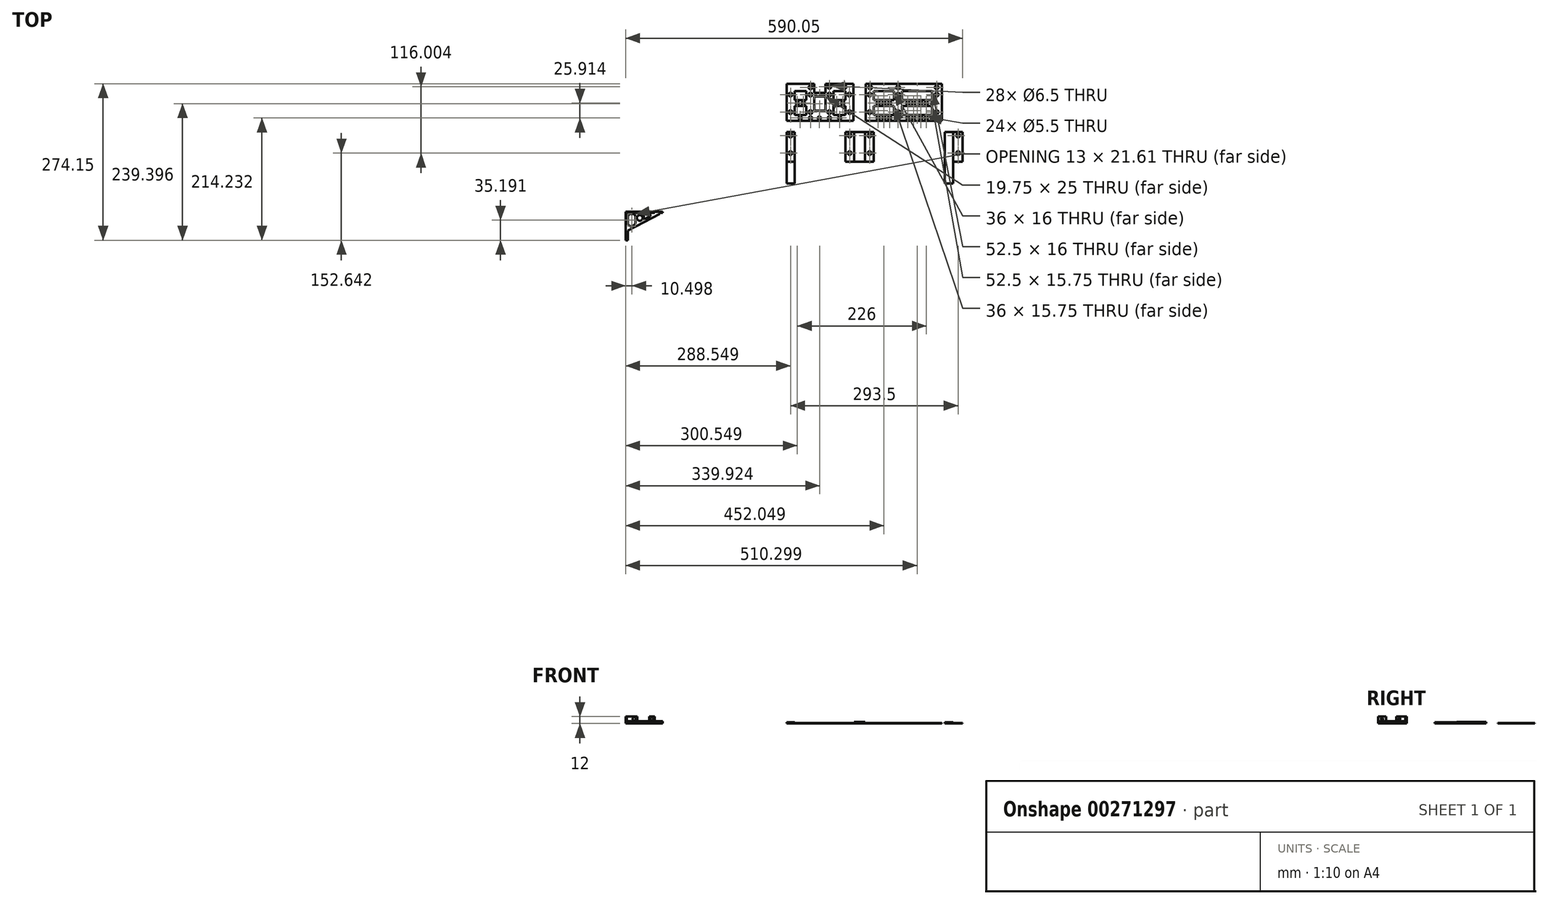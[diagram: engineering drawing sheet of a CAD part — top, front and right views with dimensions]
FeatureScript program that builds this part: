
annotation { "Feature Type Name" : "Feature", "Feature Type Description" : "" }
export const myFeature = defineFeature(function(context is Context, id is Id, definition is map)
    precondition{}
    {
        {
            var Q0;
            Q0=qCreatedBy(makeId("Top.planeOp"),FACE);
            var sketch = newSketch(context, id + "F0", { "sketchPlane" : qUnion([Q0])});
            skLineSegment(sketch, "E0.bottom", {"start": v(-67.64, 28.29) * mm, "end": v(65.86, 28.29) * mm});
            skLineSegment(sketch, "E0.left", {"start": v(-67.64, 28.29) * mm, "end": v(-67.64, 15.29) * mm});
            skLineSegment(sketch, "E0.right", {"start": v(65.86, 28.29) * mm, "end": v(65.86, 15.29) * mm});
            skCircle(sketch, "E1", {"center": v(-59.64, 21.79) * mm, "radius": 3.25 * mm});
            skCircle(sketch, "E2", {"center": v(-10.64, 21.79) * mm, "radius": 3.25 * mm});
            skCircle(sketch, "E3", {"center": v(56.86, 21.79) * mm, "radius": 3.25 * mm});
            skLineSegment(sketch, "E4.right", {"start": v(-206.14, 28.29) * mm, "end": v(-206.14, 15.29) * mm});
            skCircle(sketch, "E5", {"center": v(-164.14, 21.79) * mm, "radius": 3.25 * mm});
            skCircle(sketch, "E6", {"center": v(-131.14, 22.79) * mm, "radius": 3.25 * mm});
            skCircle(sketch, "E7", {"center": v(-104.64, 22.59) * mm, "radius": 3.25 * mm});
            skLineSegment(sketch, "E8.bottom", {"start": v(-17.64, 15.29) * mm, "end": v(-3.64, 15.29) * mm});
            skLineSegment(sketch, "E8.top", {"start": v(-17.64, -26.46) * mm, "end": v(-3.64, -26.46) * mm});
            skLineSegment(sketch, "E8.left", {"start": v(-17.64, 15.29) * mm, "end": v(-17.64, -26.46) * mm});
            skLineSegment(sketch, "E8.right", {"start": v(-3.64, 15.29) * mm, "end": v(-3.64, -26.46) * mm});
            skLineSegment(sketch, "E9.bottom", {"start": v(-67.64, 15.29) * mm, "end": v(-53.64, 15.29) * mm});
            skLineSegment(sketch, "E10.top", {"start": v(-67.64, -36.46) * mm, "end": v(65.86, -36.46) * mm});
            skLineSegment(sketch, "E11.left", {"start": v(-206.14, 15.29) * mm, "end": v(-206.14, -36.46) * mm});
            skLineSegment(sketch, "E12.top", {"start": v(-206.14, -36.46) * mm, "end": v(-89.14, -36.46) * mm});
            skLineSegment(sketch, "E13", {"start": v(-206.14, 28.29) * mm, "end": v(-157.64, 28.29) * mm});
            skLineSegment(sketch, "E14", {"start": v(-89.14, 28.29) * mm, "end": v(-137.9, 28.29) * mm});
            skLineSegment(sketch, "E15", {"start": v(-157.64, 12.54) * mm, "end": v(-137.9, 12.54) * mm});
            skLineSegment(sketch, "E16", {"start": v(-157.64, -18.96) * mm, "end": v(-137.9, -18.96) * mm});
            skLineSegment(sketch, "E17", {"start": v(-157.64, 6.04) * mm, "end": v(-137.9, 6.04) * mm});
            skLineSegment(sketch, "E18", {"start": v(-53.64, 15.29) * mm, "end": v(-17.64, 15.29) * mm});
            skLineSegment(sketch, "E19", {"start": v(-3.64, 15.29) * mm, "end": v(65.86, 15.29) * mm});
            skLineSegment(sketch, "E20", {"start": v(48.86, 15.29) * mm, "end": v(48.86, -26.46) * mm});
            skLineSegment(sketch, "E21.bottom", {"start": v(-206.14, -36.46) * mm, "end": v(-192.14, -36.46) * mm});
            skCircle(sketch, "E22", {"center": v(-199.14, -21.46) * mm, "radius": 3.25 * mm});
            skCircle(sketch, "E23", {"center": v(-199.14, 9.29) * mm, "radius": 3.25 * mm});
            skLineSegment(sketch, "E24.bottom", {"start": v(-192.14, -0.71) * mm, "end": v(-171.64, -0.71) * mm});
            skLineSegment(sketch, "E24.top", {"start": v(-192.14, -10.71) * mm, "end": v(-171.64, -10.71) * mm});
            skLineSegment(sketch, "E24.left", {"start": v(-192.14, -0.71) * mm, "end": v(-192.14, -10.71) * mm});
            skLineSegment(sketch, "E24.right", {"start": v(-171.64, -0.71) * mm, "end": v(-171.64, -10.71) * mm});
            skLineSegment(sketch, "E25", {"start": v(-206.14, 15.29) * mm, "end": v(-157.64, 15.29) * mm});
            skLineSegment(sketch, "E26", {"start": v(-89.14, 15.29) * mm, "end": v(-137.9, 15.29) * mm});
            skLineSegment(sketch, "E27", {"start": v(-171.64, -0.71) * mm, "end": v(-171.64, 15.29) * mm});
            skLineSegment(sketch, "E28", {"start": v(-171.64, -10.71) * mm, "end": v(-171.64, -26.46) * mm});
            skLineSegment(sketch, "E29", {"start": v(-123.9, 15.29) * mm, "end": v(-123.9, -26.46) * mm});
            skLineSegment(sketch, "E30", {"start": v(-157.64, 28.29) * mm, "end": v(-157.64, -18.96) * mm});
            skLineSegment(sketch, "E31", {"start": v(-137.9, 28.29) * mm, "end": v(-137.9, -18.96) * mm});
            skLineSegment(sketch, "E32", {"start": v(-137.9, -18.96) * mm, "end": v(-137.9, -26.46) * mm});
            skLineSegment(sketch, "E33", {"start": v(-157.64, -18.96) * mm, "end": v(-157.64, -26.46) * mm});
            skLineSegment(sketch, "E34", {"start": v(-123.9, -0.71) * mm, "end": v(-103.14, -0.71) * mm});
            skLineSegment(sketch, "E35", {"start": v(-123.9, -10.71) * mm, "end": v(-103.14, -10.71) * mm});
            skCircle(sketch, "E36", {"center": v(-187.14, -5.71) * mm, "radius": 2.75 * mm});
            skCircle(sketch, "E37", {"center": v(-176.64, -5.71) * mm, "radius": 2.75 * mm});
            skCircle(sketch, "E38", {"center": v(-118.47, -5.71) * mm, "radius": 2.75 * mm});
            skPoint(sketch, "E38.centerSnap0", {"position": v(-171.64, -5.71) * mm});
            skCircle(sketch, "E39", {"center": v(-107.72, -5.71) * mm, "radius": 2.75 * mm});
            skCircle(sketch, "E40", {"center": v(-96.14, 9.29) * mm, "radius": 3.25 * mm});
            skPoint(sketch, "E41.centerSnap0", {"position": v(-192.14, -5.59) * mm});
            skCircle(sketch, "E42", {"center": v(-95.64, -21.46) * mm, "radius": 3.25 * mm});
            skLineSegment(sketch, "E43", {"start": v(-53.64, -0.71) * mm, "end": v(-17.64, -0.71) * mm});
            skLineSegment(sketch, "E44", {"start": v(-53.64, -10.71) * mm, "end": v(-17.64, -10.71) * mm});
            skCircle(sketch, "E45", {"center": v(-60.64, 9.29) * mm, "radius": 3.25 * mm});
            skCircle(sketch, "E46", {"center": v(-60.64, -21.46) * mm, "radius": 3.25 * mm});
            skCircle(sketch, "E47", {"center": v(-45.64, -5.71) * mm, "radius": 2.75 * mm});
            skCircle(sketch, "E48", {"center": v(-35.64, -5.71) * mm, "radius": 2.75 * mm});
            skCircle(sketch, "E49", {"center": v(-25.64, -5.71) * mm, "radius": 2.75 * mm});
            skLineSegment(sketch, "E50", {"start": v(-3.64, -0.71) * mm, "end": v(48.86, -0.71) * mm});
            skLineSegment(sketch, "E51", {"start": v(-3.64, -10.71) * mm, "end": v(48.86, -10.71) * mm});
            skCircle(sketch, "E52", {"center": v(6.36, -5.71) * mm, "radius": 2.75 * mm});
            skCircle(sketch, "E53", {"center": v(16.36, -5.71) * mm, "radius": 2.75 * mm});
            skCircle(sketch, "E54", {"center": v(28.86, -5.71) * mm, "radius": 2.75 * mm});
            skCircle(sketch, "E55", {"center": v(38.86, -5.71) * mm, "radius": 2.75 * mm});
            skCircle(sketch, "E56", {"center": v(-10.64, 9.29) * mm, "radius": 3.25 * mm});
            skCircle(sketch, "E57", {"center": v(56.86, 9.29) * mm, "radius": 3.25 * mm});
            skCircle(sketch, "E58", {"center": v(56.86, -21.46) * mm, "radius": 3.25 * mm});
            skCircle(sketch, "E59", {"center": v(-10.64, -21.46) * mm, "radius": 3.25 * mm});
            skLineSegment(sketch, "E60.bottom", {"start": v(-88.14, -56.46) * mm, "end": v(-68.64, -56.46) * mm});
            skLineSegment(sketch, "E61.bottom", {"start": v(-206.14, -56.46) * mm, "end": v(-192.14, -56.46) * mm});
            skCircle(sketch, "E62", {"center": v(-199.14, -62.46) * mm, "radius": 3.25 * mm});
            skLineSegment(sketch, "E63.bottom", {"start": v(71.36, -56.46) * mm, "end": v(85.36, -56.46) * mm});
            skLineSegment(sketch, "E64", {"start": v(-206.14, -56.46) * mm, "end": v(-206.14, -146.46) * mm});
            skLineSegment(sketch, "E65", {"start": v(-206.14, -108.21) * mm, "end": v(-192.14, -108.21) * mm});
            skLineSegment(sketch, "E66", {"start": v(-192.14, -56.46) * mm, "end": v(-192.14, -108.21) * mm});
            skCircle(sketch, "E67", {"center": v(-199.14, -93.21) * mm, "radius": 3.25 * mm});
            skLineSegment(sketch, "E68", {"start": v(-192.14, -108.21) * mm, "end": v(-192.14, -146.46) * mm});
            skLineSegment(sketch, "E69", {"start": v(-192.14, -146.46) * mm, "end": v(-206.14, -146.46) * mm});
            skLineSegment(sketch, "E70", {"start": v(-88.14, -56.46) * mm, "end": v(-88.14, -108.21) * mm});
            skLineSegment(sketch, "E71", {"start": v(-88.14, -108.21) * mm, "end": v(-68.64, -108.21) * mm});
            skLineSegment(sketch, "E72", {"start": v(-103.14, -56.46) * mm, "end": v(-88.14, -56.46) * mm});
            skLineSegment(sketch, "E73", {"start": v(-103.14, -108.21) * mm, "end": v(-88.14, -108.21) * mm});
            skLineSegment(sketch, "E74", {"start": v(-68.64, -108.21) * mm, "end": v(-53.64, -108.21) * mm});
            skLineSegment(sketch, "E75", {"start": v(-53.64, -56.46) * mm, "end": v(-68.64, -56.46) * mm});
            skCircle(sketch, "E76", {"center": v(-95.64, -62.46) * mm, "radius": 3.25 * mm});
            skCircle(sketch, "E77", {"center": v(-95.64, -93.22) * mm, "radius": 3.25 * mm});
            skCircle(sketch, "E78", {"center": v(-60.64, -62.46) * mm, "radius": 3.25 * mm});
            skCircle(sketch, "E79", {"center": v(-60.64, -93.22) * mm, "radius": 3.25 * mm});
            skLineSegment(sketch, "E80", {"start": v(85.36, -56.46) * mm, "end": v(85.36, -146.46) * mm});
            skLineSegment(sketch, "E81", {"start": v(71.36, -56.46) * mm, "end": v(71.36, -146.46) * mm});
            skLineSegment(sketch, "E82", {"start": v(71.36, -146.46) * mm, "end": v(85.36, -146.46) * mm});
            skLineSegment(sketch, "E83", {"start": v(-192.14, -10.71) * mm, "end": v(-192.14, -36.46) * mm});
            skLineSegment(sketch, "E84", {"start": v(-192.14, -0.71) * mm, "end": v(-192.14, 15.29) * mm});
            skLineSegment(sketch, "E85", {"start": v(-103.14, -36.46) * mm, "end": v(-103.14, 15.29) * mm});
            skLineSegment(sketch, "E86", {"start": v(-192.14, -26.46) * mm, "end": v(-103.14, -26.46) * mm});
            skLineSegment(sketch, "E87", {"start": v(-89.14, 28.29) * mm, "end": v(-89.14, -36.46) * mm});
            skLineSegment(sketch, "E88", {"start": v(-103.14, -56.46) * mm, "end": v(-103.14, -108.21) * mm});
            skLineSegment(sketch, "E89", {"start": v(-68.64, -56.46) * mm, "end": v(-68.64, -108.21) * mm});
            skLineSegment(sketch, "E90", {"start": v(-53.64, -56.46) * mm, "end": v(-53.64, -108.21) * mm});
            skLineSegment(sketch, "E91", {"start": v(-67.64, 15.29) * mm, "end": v(-67.64, -36.46) * mm});
            skLineSegment(sketch, "E92", {"start": v(-53.64, 15.29) * mm, "end": v(-53.64, -36.46) * mm});
            skLineSegment(sketch, "E93", {"start": v(-17.64, -26.46) * mm, "end": v(-53.64, -26.46) * mm});
            skLineSegment(sketch, "E94", {"start": v(-3.64, -26.46) * mm, "end": v(48.86, -26.46) * mm});
            skLineSegment(sketch, "E95", {"start": v(65.86, 15.29) * mm, "end": v(65.86, -36.46) * mm});
            skLineSegment(sketch, "E96", {"start": v(-171.64, 15.29) * mm, "end": v(-171.64, 28.29) * mm});
            skLineSegment(sketch, "E97", {"start": v(-123.9, 15.29) * mm, "end": v(-123.9, 28.29) * mm});
            skLineSegment(sketch, "E98", {"start": v(85.36, -56.46) * mm, "end": v(102.36, -56.46) * mm});
            skLineSegment(sketch, "E99", {"start": v(85.36, -108.21) * mm, "end": v(102.36, -108.21) * mm});
            skLineSegment(sketch, "E100", {"start": v(102.36, -56.46) * mm, "end": v(102.36, -108.21) * mm});
            skCircle(sketch, "E101", {"center": v(94.36, -62.46) * mm, "radius": 3.25 * mm});
            skCircle(sketch, "E102", {"center": v(94.36, -93.22) * mm, "radius": 3.25 * mm});
            skLineSegment(sketch, "E103", {"start": v(48.86, -26.46) * mm, "end": v(48.86, -36.46) * mm});
            skCircle(sketch, "E104", {"center": v(-164.14, -21.46) * mm, "radius": 3.25 * mm});
            skCircle(sketch, "E105", {"center": v(-131.14, -21.46) * mm, "radius": 3.25 * mm});
            skCircle(sketch, "E106", {"center": v(-164.14, 9.29) * mm, "radius": 3.25 * mm});
            skCircle(sketch, "E107", {"center": v(-131.14, 9.29) * mm, "radius": 3.25 * mm});
            skCircle(sketch, "E108", {"center": v(-164.14, -31.63) * mm, "radius": 2.75 * mm});
            skCircle(sketch, "E109", {"center": v(-131.14, -31.63) * mm, "radius": 2.75 * mm});
            skCircle(sketch, "E110", {"center": v(-182.14, -31.63) * mm, "radius": 2.75 * mm});
            skCircle(sketch, "E111", {"center": v(-113.14, -31.63) * mm, "radius": 2.75 * mm});
            skCircle(sketch, "E112", {"center": v(-148.7, -31.63) * mm, "radius": 2.75 * mm});
            skCircle(sketch, "E113", {"center": v(-45.64, -31.63) * mm, "radius": 2.75 * mm});
            skCircle(sketch, "E114", {"center": v(-35.64, -31.63) * mm, "radius": 2.75 * mm});
            skPoint(sketch, "E114.centerSnap0", {"position": v(-35.64, -10.71) * mm});
            skCircle(sketch, "E115", {"center": v(-25.64, -31.63) * mm, "radius": 2.75 * mm});
            skCircle(sketch, "E116", {"center": v(-10.64, -31.63) * mm, "radius": 2.75 * mm});
            skPoint(sketch, "E116.centerSnap0", {"position": v(-10.64, -26.46) * mm});
            skCircle(sketch, "E117", {"center": v(6.36, -31.63) * mm, "radius": 2.75 * mm});
            skCircle(sketch, "E118", {"center": v(16.36, -31.63) * mm, "radius": 2.75 * mm});
            skCircle(sketch, "E119", {"center": v(28.86, -31.63) * mm, "radius": 2.75 * mm});
            skCircle(sketch, "E120", {"center": v(38.86, -31.63) * mm, "radius": 2.75 * mm});
            skLineSegment(sketch, "E121.top", {"start": v(-483.7, -46.52) * mm, "end": v(-369.37, -46.52) * mm});
            skLineSegment(sketch, "E121.left", {"start": v(-483.7, 31.5) * mm, "end": v(-483.7, -46.52) * mm});
            skLineSegment(sketch, "E122.left", {"start": v(-483.7, -199.86) * mm, "end": v(-483.7, -224.8) * mm});
            skLineSegment(sketch, "E123", {"start": v(-483.7, 31.5) * mm, "end": v(-369.37, -46.52) * mm});
            skLineSegment(sketch, "E124", {"start": v(-487.7, -195.86) * mm, "end": v(-487.7, -245.86) * mm});
            skLineSegment(sketch, "E125", {"start": v(-422.94, -195.86) * mm, "end": v(-487.7, -195.86) * mm});
            skLineSegment(sketch, "E126", {"start": v(-487.7, -245.86) * mm, "end": v(-483.7, -245.86) * mm});
            skLineSegment(sketch, "E127", {"start": v(-483.7, -245.86) * mm, "end": v(-483.7, -229.34) * mm});
            skLineSegment(sketch, "E128", {"start": v(-483.7, -199.86) * mm, "end": v(-428.35, -199.86) * mm});
            skLineSegment(sketch, "E129", {"start": v(-422.94, -195.86) * mm, "end": v(-422.94, -197.86) * mm});
            skLineSegment(sketch, "E130", {"start": v(-422.94, -197.86) * mm, "end": v(-428.35, -197.86) * mm});
            skLineSegment(sketch, "E131", {"start": v(-428.35, -197.86) * mm, "end": v(-428.35, -199.86) * mm});
            skLineSegment(sketch, "E132", {"start": v(-483.7, -229.34) * mm, "end": v(-428.35, -199.86) * mm});
            skLineSegment(sketch, "E133", {"start": v(-483.7, -224.8) * mm, "end": v(-436.86, -199.86) * mm});
            skCircle(sketch, "E134", {"center": v(-463.02, -206.86) * mm, "radius": 5 * mm});
            skLineSegment(sketch, "E135", {"start": v(-470.7, -199.86) * mm, "end": v(-470.7, -217.88) * mm});
            skLineSegment(sketch, "E136", {"start": v(-456.02, -199.86) * mm, "end": v(-456.02, -210.07) * mm});
            skLineSegment(sketch, "E137.left", {"start": v(-389.18, -184.17) * mm, "end": v(-389.18, -209.12) * mm});
            skLineSegment(sketch, "E138", {"start": v(-393.18, -180.17) * mm, "end": v(-393.18, -230.17) * mm});
            skLineSegment(sketch, "E139", {"start": v(-328.43, -180.17) * mm, "end": v(-393.18, -180.17) * mm});
            skLineSegment(sketch, "E140", {"start": v(-393.18, -230.17) * mm, "end": v(-389.18, -230.17) * mm});
            skLineSegment(sketch, "E141", {"start": v(-389.18, -230.17) * mm, "end": v(-389.18, -213.65) * mm});
            skLineSegment(sketch, "E142", {"start": v(-389.18, -184.17) * mm, "end": v(-333.84, -184.17) * mm});
            skLineSegment(sketch, "E143", {"start": v(-328.43, -180.17) * mm, "end": v(-328.43, -182.17) * mm});
            skLineSegment(sketch, "E144", {"start": v(-328.43, -182.17) * mm, "end": v(-333.84, -182.17) * mm});
            skLineSegment(sketch, "E145", {"start": v(-333.84, -182.17) * mm, "end": v(-333.84, -184.17) * mm});
            skLineSegment(sketch, "E146", {"start": v(-389.18, -213.65) * mm, "end": v(-333.84, -184.17) * mm});
            skLineSegment(sketch, "E147", {"start": v(-389.18, -209.12) * mm, "end": v(-342.35, -184.17) * mm});
            skCircle(sketch, "E148", {"center": v(-368.51, -191.17) * mm, "radius": 5 * mm});
            skLineSegment(sketch, "E149", {"start": v(-376.18, -184.17) * mm, "end": v(-376.18, -202.2) * mm});
            skLineSegment(sketch, "E150", {"start": v(-361.51, -184.17) * mm, "end": v(-361.51, -194.38) * mm});
            skLineSegment(sketch, "E151.left", {"start": v(-289.54, -195.88) * mm, "end": v(-289.54, -220.82) * mm});
            skLineSegment(sketch, "E152", {"start": v(-293.54, -191.88) * mm, "end": v(-293.54, -241.88) * mm});
            skLineSegment(sketch, "E153", {"start": v(-228.8, -191.88) * mm, "end": v(-293.54, -191.88) * mm});
            skLineSegment(sketch, "E154", {"start": v(-293.54, -241.88) * mm, "end": v(-289.54, -241.88) * mm});
            skLineSegment(sketch, "E155", {"start": v(-289.54, -241.88) * mm, "end": v(-289.54, -225.35) * mm});
            skLineSegment(sketch, "E156", {"start": v(-289.54, -195.88) * mm, "end": v(-234.2, -195.88) * mm});
            skLineSegment(sketch, "E157", {"start": v(-228.8, -191.88) * mm, "end": v(-228.8, -193.88) * mm});
            skLineSegment(sketch, "E158", {"start": v(-228.8, -193.88) * mm, "end": v(-234.2, -193.88) * mm});
            skLineSegment(sketch, "E159", {"start": v(-234.2, -193.88) * mm, "end": v(-234.2, -195.88) * mm});
            skLineSegment(sketch, "E160", {"start": v(-289.54, -225.35) * mm, "end": v(-234.2, -195.88) * mm});
            skLineSegment(sketch, "E161", {"start": v(-289.54, -220.82) * mm, "end": v(-242.7, -195.88) * mm});
            skCircle(sketch, "E162", {"center": v(-268.87, -202.88) * mm, "radius": 5 * mm});
            skLineSegment(sketch, "E163", {"start": v(-276.54, -195.88) * mm, "end": v(-276.54, -213.9) * mm});
            skLineSegment(sketch, "E164", {"start": v(-261.87, -195.88) * mm, "end": v(-261.87, -206.08) * mm});
            skLineSegment(sketch, "E165.left", {"start": v(-156.22, -195.88) * mm, "end": v(-156.22, -220.82) * mm});
            skLineSegment(sketch, "E166", {"start": v(-160.22, -191.88) * mm, "end": v(-160.22, -241.88) * mm});
            skLineSegment(sketch, "E167", {"start": v(-95.47, -191.88) * mm, "end": v(-160.22, -191.88) * mm});
            skLineSegment(sketch, "E168", {"start": v(-160.22, -241.88) * mm, "end": v(-156.22, -241.88) * mm});
            skLineSegment(sketch, "E169", {"start": v(-156.22, -241.88) * mm, "end": v(-156.22, -225.35) * mm});
            skLineSegment(sketch, "E170", {"start": v(-156.22, -195.88) * mm, "end": v(-100.87, -195.88) * mm});
            skLineSegment(sketch, "E171", {"start": v(-95.47, -191.88) * mm, "end": v(-95.47, -193.88) * mm});
            skLineSegment(sketch, "E172", {"start": v(-95.47, -193.88) * mm, "end": v(-100.87, -193.88) * mm});
            skLineSegment(sketch, "E173", {"start": v(-100.87, -193.88) * mm, "end": v(-100.87, -195.88) * mm});
            skLineSegment(sketch, "E174", {"start": v(-156.22, -225.35) * mm, "end": v(-100.87, -195.88) * mm});
            skLineSegment(sketch, "E175", {"start": v(-156.22, -220.82) * mm, "end": v(-109.38, -195.88) * mm});
            skCircle(sketch, "E176", {"center": v(-135.54, -202.88) * mm, "radius": 5 * mm});
            skLineSegment(sketch, "E177", {"start": v(-143.22, -195.88) * mm, "end": v(-143.22, -213.9) * mm});
            skLineSegment(sketch, "E178", {"start": v(-128.54, -195.88) * mm, "end": v(-128.54, -206.08) * mm});
            skLineSegment(sketch, "E179.left", {"start": v(-36.72, -188.78) * mm, "end": v(-36.72, -213.73) * mm});
            skLineSegment(sketch, "E180", {"start": v(-40.72, -184.78) * mm, "end": v(-40.72, -234.78) * mm});
            skLineSegment(sketch, "E181", {"start": v(24.03, -184.78) * mm, "end": v(-40.72, -184.78) * mm});
            skLineSegment(sketch, "E182", {"start": v(-40.72, -234.78) * mm, "end": v(-36.72, -234.78) * mm});
            skLineSegment(sketch, "E183", {"start": v(-36.72, -234.78) * mm, "end": v(-36.72, -218.26) * mm});
            skLineSegment(sketch, "E184", {"start": v(-36.72, -188.78) * mm, "end": v(18.63, -188.78) * mm});
            skLineSegment(sketch, "E185", {"start": v(24.03, -184.78) * mm, "end": v(24.03, -186.78) * mm});
            skLineSegment(sketch, "E186", {"start": v(24.03, -186.78) * mm, "end": v(18.63, -186.78) * mm});
            skLineSegment(sketch, "E187", {"start": v(18.63, -186.78) * mm, "end": v(18.63, -188.78) * mm});
            skLineSegment(sketch, "E188", {"start": v(-36.72, -218.26) * mm, "end": v(18.63, -188.78) * mm});
            skLineSegment(sketch, "E189", {"start": v(-36.72, -213.73) * mm, "end": v(10.12, -188.78) * mm});
            skCircle(sketch, "E190", {"center": v(-16.05, -195.78) * mm, "radius": 5 * mm});
            skLineSegment(sketch, "E191", {"start": v(-23.72, -188.78) * mm, "end": v(-23.72, -206.8) * mm});
            skLineSegment(sketch, "E192", {"start": v(-9.05, -188.78) * mm, "end": v(-9.05, -198.99) * mm});
            skSolve(sketch);
        }
        {
            var Q0;
            {var subQ3=sQuery(id+"F0.wireOp",EDGE,"E4.right");Q0=makeQuery(id+"F0.imprint","IMPRINT",FACE,{"disambiguationData":[TD([[makeQuery(id+"F0.imprint","IMPRINT",EDGE,{"derivedFrom":subQ3}),1.0]])]});}
            var Q1;
            Q1=makeQuery(id+"F0.imprint","IMPRINT",FACE,{"disambiguationData":[TD([[makeQuery(id+"F0.imprint","IMPRINT",EDGE,{"derivedFrom":sQuery(id+"F0.wireOp",EDGE,"HTkd6Cf2-wG7s-EmOn-9tAn-EZecpfU8ul1U")}),-1.0]])]});
            var Q2;
            Q2=makeQuery(id+"F0.imprint","IMPRINT",FACE,{"disambiguationData":[TD([[makeQuery(id+"F0.imprint","IMPRINT",EDGE,{"derivedFrom":sQuery(id+"F0.wireOp",EDGE,"qIvpg7tN-6wbN-jXnI-hAgA-i2ILZm4hv7hy")}),-1.0]])]});
            var Q3;
            Q3=makeQuery(id+"F0.imprint","IMPRINT",FACE,{"disambiguationData":[TD([[makeQuery(id+"F0.imprint","IMPRINT",EDGE,{"derivedFrom":sQuery(id+"F0.wireOp",EDGE,"E7")}),-1.0]])]});
            var Q4;
            {var subQ1=sQuery(id+"F0.wireOp",EDGE,"E34");Q4=makeQuery(id+"F0.imprint","IMPRINT",FACE,{"disambiguationData":[TD([[makeQuery(id+"F0.imprint","IMPRINT",EDGE,{"derivedFrom":subQ1}),-1.0]])]});}
            var Q5;
            Q5=makeQuery(id+"F0.imprint","IMPRINT",FACE,{"disambiguationData":[TD([[makeQuery(id+"F0.imprint","IMPRINT",EDGE,{"derivedFrom":sQuery(id+"F0.wireOp",EDGE,"hdawPmHm-zHTX-q96l-AVKO-EE5j0ArRiJjP")}),-1.0]])]});
            var Q6;
            {var subQ4=sQuery(id+"F0.wireOp",EDGE,"E85");var subQ5=sQuery(id+"F0.wireOp",EDGE,"E12.top");var subQ6=makeQuery(id+"F0.imprint","INTERSECT",VERTEX,{"derivedFrom":[subQ5,subQ4]});Q6=makeQuery(id+"F0.imprint","IMPRINT",FACE,{"disambiguationData":[TD([[makeQuery(id+"F0.imprint","IMPRINT",EDGE,{"disambiguationData":[TD([[subQ6,-1.0]])],"derivedFrom":subQ4}),1.0]])]});}
            var Q7;
            Q7=makeQuery(id+"F0.imprint","IMPRINT",FACE,{"disambiguationData":[TD([[makeQuery(id+"F0.imprint","IMPRINT",EDGE,{"derivedFrom":sQuery(id+"F0.wireOp",EDGE,"E16")}),-1.0]])]});
            var Q8;
            {var subQ0=sQuery(id+"F0.wireOp",EDGE,"E15");Q8=makeQuery(id+"F0.imprint","IMPRINT",FACE,{"disambiguationData":[TD([[makeQuery(id+"F0.imprint","IMPRINT",EDGE,{"derivedFrom":subQ0}),-1.0]])]});}
            var Q9;
            Q9=makeQuery(id+"F0.imprint","IMPRINT",FACE,{"disambiguationData":[TD([[makeQuery(id+"F0.imprint","IMPRINT",EDGE,{"derivedFrom":sQuery(id+"F0.wireOp",EDGE,"6AZQfdwE-rYJR-m2Ky-hR9G-nS1HAU66PkIi")}),-1.0]])]});
            var Q10;
            Q10=makeQuery(id+"F0.imprint","IMPRINT",FACE,{"disambiguationData":[TD([[makeQuery(id+"F0.imprint","IMPRINT",EDGE,{"derivedFrom":sQuery(id+"F0.wireOp",EDGE,"E24.bottom")}),-1.0]])]});
            var Q11;
            Q11=makeQuery(id+"F0.imprint","IMPRINT",FACE,{"disambiguationData":[TD([[makeQuery(id+"F0.imprint","IMPRINT",EDGE,{"derivedFrom":sQuery(id+"F0.wireOp",EDGE,"E0.bottom")}),-1.0]])]});
            var Q12;
            {var subQ1=sQuery(id+"F0.wireOp",EDGE,"E50");Q12=makeQuery(id+"F0.imprint","IMPRINT",FACE,{"disambiguationData":[TD([[makeQuery(id+"F0.imprint","IMPRINT",EDGE,{"derivedFrom":subQ1}),-1.0]])]});}
            var Q13;
            Q13=makeQuery(id+"F0.imprint","IMPRINT",FACE,{"disambiguationData":[TD([[makeQuery(id+"F0.imprint","IMPRINT",EDGE,{"derivedFrom":sQuery(id+"F0.wireOp",EDGE,"E8.top")}),-1.0]])]});
            var Q14;
            {var subQ3=sQuery(id+"F0.wireOp",EDGE,"E8.bottom");Q14=makeQuery(id+"F0.imprint","IMPRINT",FACE,{"disambiguationData":[TD([[makeQuery(id+"F0.imprint","IMPRINT",EDGE,{"derivedFrom":subQ3}),-1.0]])]});}
            var Q15;
            {var subQ1=sQuery(id+"F0.wireOp",EDGE,"E43");Q15=makeQuery(id+"F0.imprint","IMPRINT",FACE,{"disambiguationData":[TD([[makeQuery(id+"F0.imprint","IMPRINT",EDGE,{"derivedFrom":subQ1}),-1.0]])]});}
            var Q16;
            {var subQ2=sQuery(id+"F0.wireOp",EDGE,"E65");Q16=makeQuery(id+"F0.imprint","IMPRINT",FACE,{"disambiguationData":[TD([[makeQuery(id+"F0.imprint","IMPRINT",EDGE,{"derivedFrom":subQ2}),-1.0]])]});}
            var Q17;
            {var subQ1=sQuery(id+"F0.wireOp",EDGE,"E61.bottom");Q17=makeQuery(id+"F0.imprint","IMPRINT",FACE,{"disambiguationData":[TD([[makeQuery(id+"F0.imprint","IMPRINT",EDGE,{"derivedFrom":subQ1}),-1.0]])]});}
            var Q18;
            Q18=makeQuery(id+"F0.imprint","IMPRINT",FACE,{"disambiguationData":[TD([[makeQuery(id+"F0.imprint","IMPRINT",EDGE,{"derivedFrom":sQuery(id+"F0.wireOp",EDGE,"E70")}),-1.0]])]});
            var Q19;
            Q19=makeQuery(id+"F0.imprint","IMPRINT",FACE,{"disambiguationData":[TD([[makeQuery(id+"F0.imprint","IMPRINT",EDGE,{"derivedFrom":sQuery(id+"F0.wireOp",EDGE,"E74")}),1.0]])]});
            var Q20;
            {var subQ3=sQuery(id+"F0.wireOp",EDGE,"E63.bottom");Q20=makeQuery(id+"F0.imprint","IMPRINT",FACE,{"disambiguationData":[TD([[makeQuery(id+"F0.imprint","IMPRINT",EDGE,{"derivedFrom":subQ3}),-1.0]])]});}
            var Q21;
            Q21=makeQuery(id+"F0.imprint","IMPRINT",FACE,{"disambiguationData":[TD([[makeQuery(id+"F0.imprint","IMPRINT",EDGE,{"derivedFrom":sQuery(id+"F0.wireOp",EDGE,"E24.right")}),1.0]])]});
            var Q22;
            Q22=makeQuery(id+"F0.imprint","IMPRINT",FACE,{"disambiguationData":[TD([[makeQuery(id+"F0.imprint","IMPRINT",EDGE,{"derivedFrom":sQuery(id+"F0.wireOp",EDGE,"E5")}),-1.0]])]});
            var Q23;
            Q23=makeQuery(id+"F0.imprint","IMPRINT",FACE,{"disambiguationData":[TD([[makeQuery(id+"F0.imprint","IMPRINT",EDGE,{"derivedFrom":sQuery(id+"F0.wireOp",EDGE,"E6")}),-1.0]])]});
            var Q24;
            {var subQ5=sQuery(id+"F0.wireOp",EDGE,"E32");Q24=makeQuery(id+"F0.imprint","IMPRINT",FACE,{"disambiguationData":[TD([[makeQuery(id+"F0.imprint","IMPRINT",EDGE,{"derivedFrom":subQ5}),1.0]])]});}
            var Q25;
            Q25=makeQuery(id+"F0.imprint","IMPRINT",FACE,{"disambiguationData":[TD([[makeQuery(id+"F0.imprint","IMPRINT",EDGE,{"derivedFrom":sQuery(id+"F0.wireOp",EDGE,"E60.bottom")}),-1.0]])]});
            var Q26;
            {var subQ0=sQuery(id+"F0.wireOp",EDGE,"E98");Q26=makeQuery(id+"F0.imprint","IMPRINT",FACE,{"disambiguationData":[TD([[makeQuery(id+"F0.imprint","IMPRINT",EDGE,{"derivedFrom":subQ0}),-1.0]])]});}
            var Q27;
            Q27=makeQuery(id+"F0.imprint","IMPRINT",FACE,{"disambiguationData":[TD([[makeQuery(id+"F0.imprint","IMPRINT",EDGE,{"derivedFrom":sQuery(id+"F0.wireOp",EDGE,"E57")}),-1.0]])]});
            var Q28;
            {var subQ4=sQuery(id+"F0.wireOp",EDGE,"E9.bottom");Q28=makeQuery(id+"F0.imprint","IMPRINT",FACE,{"disambiguationData":[TD([[makeQuery(id+"F0.imprint","IMPRINT",EDGE,{"derivedFrom":subQ4}),-1.0]])]});}
            var Q29;
            Q29=makeQuery(id+"F0.imprint","IMPRINT",FACE,{"disambiguationData":[TD([[makeQuery(id+"F0.imprint","IMPRINT",EDGE,{"derivedFrom":sQuery(id+"F0.wireOp",EDGE,"E40")}),-1.0]])]});
            var Q30;
            {var subQ4=sQuery(id+"F0.wireOp",EDGE,"E11.left");Q30=makeQuery(id+"F0.imprint","IMPRINT",FACE,{"disambiguationData":[TD([[makeQuery(id+"F0.imprint","IMPRINT",EDGE,{"derivedFrom":subQ4}),1.0]])]});}
            extrude(context, id + "F1", {"entities" : qUnion([Q0, Q1, Q2, Q3, Q4, Q5, Q6, Q7, Q8, Q9, Q10, Q11, Q12, Q13, Q14, Q15, Q16, Q17, Q18, Q19, Q20, Q21, Q22, Q23, Q24, Q25, Q26, Q27, Q28, Q29, Q30]), "depth" : 1 * mm});
        }
        {
            var Q0;
            Q0=makeQuery(id+"F1.opExtrude","CAP_FACE",FACE,{"disambiguationData":[OSD([sQuery(id+"F0.wireOp",EDGE,"E61.bottom"),sQuery(id+"F0.wireOp",EDGE,"E62"),sQuery(id+"F0.wireOp",EDGE,"E64"),sQuery(id+"F0.wireOp",EDGE,"E66"),sQuery(id+"F0.wireOp",EDGE,"E67"),sQuery(id+"F0.wireOp",EDGE,"E68"),sQuery(id+"F0.wireOp",EDGE,"E69")])],"isStart":false});
            var sketch = newSketch(context, id + "F2", { "sketchPlane" : qUnion([Q0])});
            skLineSegment(sketch, "E193.bottom", {"start": v(-206.14, -108.48) * mm, "end": v(-192.14, -108.48) * mm});
            skLineSegment(sketch, "E193.top", {"start": v(-206.14, -146.46) * mm, "end": v(-192.14, -146.46) * mm});
            skLineSegment(sketch, "E193.left", {"start": v(-206.14, -108.48) * mm, "end": v(-206.14, -146.46) * mm});
            skLineSegment(sketch, "E193.right", {"start": v(-192.14, -108.48) * mm, "end": v(-192.14, -146.46) * mm});
            skSolve(sketch);
        }
        {
            var Q0;
            Q0=makeQuery(id+"F1.opExtrude","CAP_FACE",FACE,{"disambiguationData":[OSD([sQuery(id+"F0.wireOp",EDGE,"E60.bottom"),sQuery(id+"F0.wireOp",EDGE,"E71"),sQuery(id+"F0.wireOp",EDGE,"E72"),sQuery(id+"F0.wireOp",EDGE,"E73"),sQuery(id+"F0.wireOp",EDGE,"E74"),sQuery(id+"F0.wireOp",EDGE,"E75"),sQuery(id+"F0.wireOp",EDGE,"E76"),sQuery(id+"F0.wireOp",EDGE,"E77"),sQuery(id+"F0.wireOp",EDGE,"E78"),sQuery(id+"F0.wireOp",EDGE,"E79"),sQuery(id+"F0.wireOp",EDGE,"E88"),sQuery(id+"F0.wireOp",EDGE,"E90")])],"isStart":false});
            var sketch = newSketch(context, id + "F3", { "sketchPlane" : qUnion([Q0])});
            skLineSegment(sketch, "E194.bottom", {"start": v(-87.96, -56.46) * mm, "end": v(-68.46, -56.46) * mm});
            skLineSegment(sketch, "E194.top", {"start": v(-87.96, -108.21) * mm, "end": v(-68.46, -108.21) * mm});
            skLineSegment(sketch, "E194.left", {"start": v(-87.96, -56.46) * mm, "end": v(-87.96, -108.21) * mm});
            skLineSegment(sketch, "E194.right", {"start": v(-68.46, -56.46) * mm, "end": v(-68.46, -108.21) * mm});
            skSolve(sketch);
        }
        {
            var Q0;
            Q0=makeQuery(id+"F1.opExtrude","CAP_FACE",FACE,{"disambiguationData":[OSD([sQuery(id+"F0.wireOp",EDGE,"E63.bottom"),sQuery(id+"F0.wireOp",EDGE,"E80"),sQuery(id+"F0.wireOp",EDGE,"E81"),sQuery(id+"F0.wireOp",EDGE,"E82"),sQuery(id+"F0.wireOp",EDGE,"E98"),sQuery(id+"F0.wireOp",EDGE,"E99"),sQuery(id+"F0.wireOp",EDGE,"E100"),sQuery(id+"F0.wireOp",EDGE,"E101"),sQuery(id+"F0.wireOp",EDGE,"E102")])],"isStart":false});
            var sketch = newSketch(context, id + "F4", { "sketchPlane" : qUnion([Q0])});
            skLineSegment(sketch, "E195.bottom", {"start": v(85.36, -56.46) * mm, "end": v(102.36, -56.46) * mm});
            skLineSegment(sketch, "E195.top", {"start": v(85.36, -108.21) * mm, "end": v(102.36, -108.21) * mm});
            skLineSegment(sketch, "E195.left", {"start": v(85.36, -56.46) * mm, "end": v(85.36, -108.21) * mm});
            skLineSegment(sketch, "E195.right", {"start": v(102.36, -56.46) * mm, "end": v(102.36, -108.21) * mm});
            skSolve(sketch);
        }
        {
            var Q0;
            Q0=makeQuery(id+"F2.imprint","IMPRINT",FACE,{"disambiguationData":[TD([[makeQuery(id+"F2.imprint","IMPRINT",EDGE,{"derivedFrom":sQuery(id+"F2.wireOp",EDGE,"E193.bottom")}),-1.0]])]});
            extrude(context, id + "F5", {"entities" : qUnion([Q0]), "operationType" : NewBodyOperationType.ADD, "depth" : 1 * mm});
        }
        {
            var Q0;
            {var subQ3=sQuery(id+"F4.wireOp",EDGE,"E195.left");Q0=makeQuery(id+"F4.imprint","IMPRINT",FACE,{"disambiguationData":[TD([[makeQuery(id+"F4.imprint","IMPRINT",EDGE,{"derivedFrom":subQ3}),-1.0]])]});}
            extrude(context, id + "F6", {"entities" : qUnion([Q0]), "operationType" : NewBodyOperationType.ADD, "depth" : 1 * mm});
        }
        {
            var Q0;
            Q0=makeQuery(id+"F3.imprint","IMPRINT",FACE,{"disambiguationData":[TD([[makeQuery(id+"F3.imprint","IMPRINT",EDGE,{"derivedFrom":sQuery(id+"F3.wireOp",EDGE,"E194.bottom")}),-1.0]])]});
            extrude(context, id + "F7", {"entities" : qUnion([Q0]), "operationType" : NewBodyOperationType.ADD, "depth" : 2 * mm});
        }
        {
            var Q0;
            {var subQ0=sQuery(id+"F0.wireOp",EDGE,"E122.left");Q0=makeQuery(id+"F0.imprint","IMPRINT",FACE,{"disambiguationData":[TD([[makeQuery(id+"F0.imprint","IMPRINT",EDGE,{"derivedFrom":subQ0}),-1.0]])]});}
            var Q1;
            {var subQ0=sQuery(id+"F0.wireOp",EDGE,"Y5QnWEah-zgKl-GyQd-s9XB-KKXOhy98gsUz");Q1=makeQuery(id+"F0.imprint","IMPRINT",FACE,{"disambiguationData":[TD([[makeQuery(id+"F0.imprint","IMPRINT",EDGE,{"derivedFrom":subQ0}),-1.0]])]});}
            var Q2;
            {var subQ0=sQuery(id+"F0.wireOp",EDGE,"QVRn6pix-hFmG-4Xx8-XSQO-IpXES93qGK1I");Q2=makeQuery(id+"F0.imprint","IMPRINT",FACE,{"disambiguationData":[TD([[makeQuery(id+"F0.imprint","IMPRINT",EDGE,{"derivedFrom":subQ0}),1.0]])]});}
            var Q3;
            Q3=makeQuery(id+"F0.imprint","IMPRINT",FACE,{"disambiguationData":[TD([[makeQuery(id+"F0.imprint","IMPRINT",EDGE,{"derivedFrom":sQuery(id+"F0.wireOp",EDGE,"E134")}),-1.0]])]});
            extrude(context, id + "F8", {"entities" : qUnion([Q0, Q1, Q2, Q3]), "depth" : 4 * mm});
        }
        {
            var Q0;
            Q0=makeQuery(id+"F8.opExtrude","CAP_FACE",FACE,{"disambiguationData":[OSD([sQuery(id+"F0.wireOp",EDGE,"E122.bottom"),sQuery(id+"F0.wireOp",EDGE,"E122.left"),sQuery(id+"F0.wireOp",EDGE,"ZlZntgY3-O136-qQlq-7laL-xEvnqNMt5ie8"),sQuery(id+"F0.wireOp",EDGE,"E124"),sQuery(id+"F0.wireOp",EDGE,"E125"),sQuery(id+"F0.wireOp",EDGE,"Y5QnWEah-zgKl-GyQd-s9XB-KKXOhy98gsUz"),sQuery(id+"F0.wireOp",EDGE,"QVRn6pix-hFmG-4Xx8-XSQO-IpXES93qGK1I"),sQuery(id+"F0.wireOp",EDGE,"RtAwYwaI-YGaJ-88zm-UU2x-KzlYEcnNuSRs"),sQuery(id+"F0.wireOp",EDGE,"OGC4cYvw-BD9B-RK5z-ryjz-SiwkxSMMCXk9")])],"isStart":false});
            var sketch = newSketch(context, id + "F9", { "sketchPlane" : qUnion([Q0])});
            skLineSegment(sketch, "E196.bottom", {"start": v(-487.7, -195.86) * mm, "end": v(-485.7, -195.86) * mm});
            skLineSegment(sketch, "E196.top", {"start": v(-487.7, -213.86) * mm, "end": v(-485.7, -213.86) * mm});
            skLineSegment(sketch, "E196.left", {"start": v(-487.7, -195.86) * mm, "end": v(-487.7, -213.86) * mm});
            skLineSegment(sketch, "E196.right", {"start": v(-485.7, -195.86) * mm, "end": v(-485.7, -213.86) * mm});
            skLineSegment(sketch, "E197.bottom", {"start": v(-485.7, -197.86) * mm, "end": v(-467.7, -197.86) * mm});
            skLineSegment(sketch, "E197.top", {"start": v(-485.7, -195.86) * mm, "end": v(-467.7, -195.86) * mm});
            skLineSegment(sketch, "E197.left", {"start": v(-485.7, -197.86) * mm, "end": v(-485.7, -195.86) * mm});
            skLineSegment(sketch, "E197.right", {"start": v(-467.7, -197.86) * mm, "end": v(-467.7, -195.86) * mm});
            skLineSegment(sketch, "E198.bottom", {"start": v(-487.7, -245.86) * mm, "end": v(-485.7, -245.86) * mm});
            skLineSegment(sketch, "E198.top", {"start": v(-487.7, -231.86) * mm, "end": v(-485.7, -231.86) * mm});
            skLineSegment(sketch, "E198.left", {"start": v(-487.7, -245.86) * mm, "end": v(-487.7, -231.86) * mm});
            skLineSegment(sketch, "E198.right", {"start": v(-485.7, -245.86) * mm, "end": v(-485.7, -231.86) * mm});
            skLineSegment(sketch, "E199.bottom", {"start": v(-446.7, -195.86) * mm, "end": v(-436.7, -195.86) * mm});
            skLineSegment(sketch, "E199.top", {"start": v(-446.7, -197.86) * mm, "end": v(-436.7, -197.86) * mm});
            skLineSegment(sketch, "E199.left", {"start": v(-446.7, -195.86) * mm, "end": v(-446.7, -197.86) * mm});
            skLineSegment(sketch, "E199.right", {"start": v(-436.7, -195.86) * mm, "end": v(-436.7, -197.86) * mm});
            skSolve(sketch);
        }
        {
            var Q0;
            {var subQ1=sQuery(id+"F9.wireOp",EDGE,"E196.bottom");Q0=makeQuery(id+"F9.imprint","IMPRINT",FACE,{"disambiguationData":[TD([[makeQuery(id+"F9.imprint","IMPRINT",EDGE,{"derivedFrom":subQ1}),1.0]])]});}
            var Q1;
            {var subQ0=sQuery(id+"F9.wireOp",EDGE,"E197.bottom");Q1=makeQuery(id+"F9.imprint","IMPRINT",FACE,{"disambiguationData":[TD([[makeQuery(id+"F9.imprint","IMPRINT",EDGE,{"derivedFrom":subQ0}),1.0]])]});}
            var Q2;
            Q2=makeQuery(id+"F9.imprint","IMPRINT",FACE,{"disambiguationData":[TD([[makeQuery(id+"F9.imprint","IMPRINT",EDGE,{"derivedFrom":sQuery(id+"F9.wireOp",EDGE,"E199.bottom")}),-1.0]])]});
            var Q3;
            {var subQ0=sQuery(id+"F9.wireOp",EDGE,"ujH1gitN-81UE-f3aj-gJf1-JRtf2pK9u4nv.top");Q3=makeQuery(id+"F9.imprint","IMPRINT",FACE,{"disambiguationData":[TD([[makeQuery(id+"F9.imprint","IMPRINT",EDGE,{"derivedFrom":subQ0}),-1.0]])]});}
            var Q4;
            Q4=makeQuery(id+"F9.imprint","IMPRINT",FACE,{"disambiguationData":[TD([[makeQuery(id+"F9.imprint","IMPRINT",EDGE,{"derivedFrom":sQuery(id+"F9.wireOp",EDGE,"I0GwsSN8-leNo-cBJJ-Puyd-Mmj1ePseNuiN")}),-1.0]])]});
            var Q5;
            Q5=makeQuery(id+"F9.imprint","IMPRINT",FACE,{"disambiguationData":[TD([[makeQuery(id+"F9.imprint","IMPRINT",EDGE,{"derivedFrom":sQuery(id+"F9.wireOp",EDGE,"WWTWJyJd-qydm-uIPr-HuiC-kHgNeHefWNs2")}),-1.0]])]});
            var Q6;
            Q6=makeQuery(id+"F9.imprint","IMPRINT",FACE,{"disambiguationData":[TD([[makeQuery(id+"F9.imprint","IMPRINT",EDGE,{"derivedFrom":sQuery(id+"F9.wireOp",EDGE,"E198.bottom")}),1.0]])]});
            var Q7;
            Q7=makeQuery(id+"F9.imprint","IMPRINT",FACE,{"disambiguationData":[TD([[makeQuery(id+"F9.imprint","IMPRINT",EDGE,{"derivedFrom":sQuery(id+"F9.wireOp",EDGE,"E199.bottom")}),1.0]])]});
            extrude(context, id + "F10", {"entities" : qUnion([Q0, Q1, Q2, Q3, Q4, Q5, Q6, Q7]), "operationType" : NewBodyOperationType.ADD, "depth" : 8 * mm});
        }
        {
            var Q0;
            Q0=makeQuery(id+"F10.boolean.opBoolean","MERGE",FACE,{"derivedFrom":[makeQuery(id+"F8.opExtrude","SWEPT_FACE",FACE,{"disambiguationData":[OSD([sQuery(id+"F0.wireOp",EDGE,"E124")])]}),makeQuery(id+"F10.opExtrude","SWEPT_FACE",FACE,{"disambiguationData":[OSD([sQuery(id+"F9.wireOp",EDGE,"E196.left")])]}),makeQuery(id+"F10.opExtrude","SWEPT_FACE",FACE,{"disambiguationData":[OSD([sQuery(id+"F9.wireOp",EDGE,"E198.left")])]})]});
            var sketch = newSketch(context, id + "F11", { "sketchPlane" : qUnion([Q0])});
            skLineSegment(sketch, "E200.bottom", {"start": v(195.86, 4) * mm, "end": v(213.86, 4) * mm});
            skLineSegment(sketch, "E200.top", {"start": v(195.86, 12) * mm, "end": v(213.86, 12) * mm});
            skLineSegment(sketch, "E200.left", {"start": v(195.86, 4) * mm, "end": v(195.86, 12) * mm});
            skLineSegment(sketch, "E200.right", {"start": v(213.86, 4) * mm, "end": v(213.86, 12) * mm});
            skLineSegment(sketch, "E201.bottom", {"start": v(245.86, 12) * mm, "end": v(231.86, 12) * mm});
            skLineSegment(sketch, "E201.top", {"start": v(245.86, 4) * mm, "end": v(231.86, 4) * mm});
            skLineSegment(sketch, "E201.left", {"start": v(245.86, 12) * mm, "end": v(245.86, 4) * mm});
            skLineSegment(sketch, "E201.right", {"start": v(231.86, 12) * mm, "end": v(231.86, 4) * mm});
            skCircle(sketch, "E202", {"center": v(208.86, 8) * mm, "radius": 1.75 * mm});
            skCircle(sketch, "E203", {"center": v(238.86, 8) * mm, "radius": 1.75 * mm});
            skSolve(sketch);
        }
        {
            var Q0;
            Q0=makeQuery(id+"F11.imprint","IMPRINT",FACE,{"disambiguationData":[TD([[makeQuery(id+"F11.imprint","IMPRINT",EDGE,{"derivedFrom":sQuery(id+"F11.wireOp",EDGE,"E202")}),1.0]])]});
            var Q1;
            Q1=makeQuery(id+"F11.imprint","IMPRINT",FACE,{"disambiguationData":[TD([[makeQuery(id+"F11.imprint","IMPRINT",EDGE,{"derivedFrom":sQuery(id+"F11.wireOp",EDGE,"E203")}),1.0]])]});
            extrude(context, id + "F12", {"entities" : qUnion([Q0, Q1]), "operationType" : NewBodyOperationType.REMOVE, "oppositeDirection" : true, "depth" : 4 * mm});
        }
        {
            var Q0;
            Q0=makeQuery(id+"F10.boolean.opBoolean","MERGE",FACE,{"derivedFrom":[makeQuery(id+"F8.opExtrude","SWEPT_FACE",FACE,{"disambiguationData":[OSD([sQuery(id+"F0.wireOp",EDGE,"E125")])]}),makeQuery(id+"F10.opExtrude","SWEPT_FACE",FACE,{"disambiguationData":[OSD([sQuery(id+"F9.wireOp",EDGE,"E196.bottom"),sQuery(id+"F9.wireOp",EDGE,"E197.top")])]}),makeQuery(id+"F10.opExtrude","SWEPT_FACE",FACE,{"disambiguationData":[OSD([sQuery(id+"F9.wireOp",EDGE,"E199.bottom")])]})]});
            var sketch = newSketch(context, id + "F13", { "sketchPlane" : qUnion([Q0])});
            skLineSegment(sketch, "E204.bottom", {"start": v(436.7, 12) * mm, "end": v(446.7, 12) * mm});
            skLineSegment(sketch, "E204.top", {"start": v(436.7, 4) * mm, "end": v(446.7, 4) * mm});
            skLineSegment(sketch, "E204.left", {"start": v(436.7, 12) * mm, "end": v(436.7, 4) * mm});
            skLineSegment(sketch, "E204.right", {"start": v(446.7, 12) * mm, "end": v(446.7, 4) * mm});
            skPoint(sketch, "E205.oppositeSnap0", {"position": v(487.7, 6) * mm});
            skLineSegment(sketch, "E205.bottom", {"start": v(467.7, 12) * mm, "end": v(487.7, 12) * mm});
            skLineSegment(sketch, "E205.top", {"start": v(467.7, 4) * mm, "end": v(487.7, 4) * mm});
            skLineSegment(sketch, "E205.left", {"start": v(467.7, 12) * mm, "end": v(467.7, 4) * mm});
            skLineSegment(sketch, "E205.right", {"start": v(487.7, 12) * mm, "end": v(487.7, 4) * mm});
            skCircle(sketch, "E206", {"center": v(441.94, 8) * mm, "radius": 2.75 * mm});
            skCircle(sketch, "E207", {"center": v(472.7, 8) * mm, "radius": 2.75 * mm});
            skSolve(sketch);
        }
        {
            var Q0;
            Q0=makeQuery(id+"F13.imprint","IMPRINT",FACE,{"disambiguationData":[TD([[makeQuery(id+"F13.imprint","IMPRINT",EDGE,{"derivedFrom":sQuery(id+"F13.wireOp",EDGE,"E206")}),1.0]])]});
            var Q1;
            Q1=makeQuery(id+"F13.imprint","IMPRINT",FACE,{"disambiguationData":[TD([[makeQuery(id+"F13.imprint","IMPRINT",EDGE,{"derivedFrom":sQuery(id+"F13.wireOp",EDGE,"E207")}),1.0]])]});
            extrude(context, id + "F14", {"entities" : qUnion([Q0, Q1]), "operationType" : NewBodyOperationType.REMOVE, "oppositeDirection" : true, "depth" : 2 * mm});
        }
        {
            var Q0;
            Q0=makeQuery(id+"F10.opExtrude","SWEPT_EDGE",EDGE,{"disambiguationData":[OSD([sQuery(id+"F9.wireOp",EDGE,"E196.right"),sQuery(id+"F9.wireOp",EDGE,"E197.bottom"),sQuery(id+"F9.wireOp",EDGE,"E197.left")])]});
            var Q1;
            Q1=makeQuery(id+"F10.opExtrude","CAP_EDGE",EDGE,{"disambiguationData":[OSD([sQuery(id+"F9.wireOp",EDGE,"E197.right")])],"isStart":true});
            var Q2;
            Q2=makeQuery(id+"F10.opExtrude","CAP_EDGE",EDGE,{"disambiguationData":[OSD([sQuery(id+"F9.wireOp",EDGE,"E199.right")])],"isStart":true});
            var Q3;
            Q3=makeQuery(id+"F10.opExtrude","CAP_EDGE",EDGE,{"disambiguationData":[OSD([sQuery(id+"F9.wireOp",EDGE,"E199.left")])],"isStart":true});
            var Q4;
            Q4=makeQuery(id+"F8.opExtrude","SWEPT_EDGE",EDGE,{"disambiguationData":[OSD([sQuery(id+"F0.wireOp",EDGE,"E122.left"),sQuery(id+"F0.wireOp",EDGE,"E128")])]});
            var Q5;
            Q5=makeQuery(id+"F8.opExtrude","SWEPT_EDGE",EDGE,{"disambiguationData":[OSD([sQuery(id+"F0.wireOp",EDGE,"E128"),sQuery(id+"F0.wireOp",EDGE,"E135")])]});
            var Q6;
            Q6=makeQuery(id+"F8.opExtrude","SWEPT_EDGE",EDGE,{"disambiguationData":[OSD([sQuery(id+"F0.wireOp",EDGE,"E133"),sQuery(id+"F0.wireOp",EDGE,"E135")])]});
            var Q7;
            Q7=makeQuery(id+"F8.opExtrude","SWEPT_EDGE",EDGE,{"disambiguationData":[OSD([sQuery(id+"F0.wireOp",EDGE,"E122.left"),sQuery(id+"F0.wireOp",EDGE,"E133")])]});
            var Q8;
            Q8=makeQuery(id+"F10.opExtrude","CAP_EDGE",EDGE,{"disambiguationData":[OSD([sQuery(id+"F9.wireOp",EDGE,"E196.top")])],"isStart":true});
            var Q9;
            Q9=makeQuery(id+"F10.opExtrude","CAP_EDGE",EDGE,{"disambiguationData":[OSD([sQuery(id+"F9.wireOp",EDGE,"E198.top")])],"isStart":true});
            fillet(context, id + "F15", {"entities" : qUnion([Q0, Q1, Q2, Q3, Q4, Q5, Q6, Q7, Q8, Q9]), "radius" : 5 * mm, "tangentPropagation" : true, "allowEdgeOverflow" : false});
        }
        {
            var Q0;
            Q0=makeQuery(id+"F8.opExtrude","SWEPT_EDGE",EDGE,{"disambiguationData":[OSD([sQuery(id+"F0.wireOp",EDGE,"E128"),sQuery(id+"F0.wireOp",EDGE,"E136")])]});
            var Q1;
            Q1=makeQuery(id+"F8.opExtrude","SWEPT_EDGE",EDGE,{"disambiguationData":[OSD([sQuery(id+"F0.wireOp",EDGE,"E133"),sQuery(id+"F0.wireOp",EDGE,"E136")])]});
            var Q2;
            Q2=makeQuery(id+"F8.opExtrude","SWEPT_EDGE",EDGE,{"disambiguationData":[OSD([sQuery(id+"F0.wireOp",EDGE,"E128"),sQuery(id+"F0.wireOp",EDGE,"E133")])]});
            fillet(context, id + "F16", {"entities" : qUnion([Q0, Q1, Q2]), "radius" : 2.5 * mm, "tangentPropagation" : true, "allowEdgeOverflow" : false});
        }
    });
